# Revit family: ЭВАН ЭПВН 9,45-18 кВт
name_source: partatom
category: Оборудование
units: mm (PartAtom-declared; Revit-internal decimal feet)

## family parameters
Всегда вертикально = Да
Классификация = Нет
На основе рабочей плоскости = Да
Общий = Нет
При загрузке вырезать с полостями = Нет
Размер круглого соединителя = Использовать диаметр
Тип детали = Нормальный
Точка расчета площади = Нет

## types (4) — shared parameters
ADSK_Классификация нагрузок = Прочее
ADSK_Материал = Сталь
ADSK_Номинальная мощность = 0 Вт
ADSK_Размер_Высота = 346 мм
ADSK_Размер_Длина = 634 мм
ADSK_Размер_Ширина = 327 мм
Dn = 16 мм
База = ЭЛЕКТРИЧЕСКИЙ ТЕПЛОГЕНЕРАТОР (КОТЕЛ)
Крышка_Видимость = Да
Материал корпуса = Сталь
Минимально допустимое давление допустимое на входе в водонагреватель, МПа = 0.02
Мощность 1-й ступени (по умолчанию) = 0 Вт
Объем колбы котла, л = 7.5
Рабоча зона_Видимость = Да
Резьба патрубков для подключения трубопроводов теплоносителя = G 1/2
zero-valued in all types: Отметка по умолчанию

## per-type parameters (varying)
| type | ADSK_Количество фаз | ADSK_Расход теплоносителя | Максимальная температура теплоносителя, оС | Потребляемая электрическая мощность при максимальной тепловой мощность  в час, кВт/ч |
| ЭВАН ЭПВН - 9.45 кВт | 1 | 0.2 м³/ч | +65 | 7.87 |
| ЭВАН ЭПВН - 12 кВт | 3 | 0.3 м³/ч | +70 | 12.6 |
| ЭВАН ЭПВН - 15 кВт | 3 | 0.4 м³/ч | +67 | 15.75 |
| ЭВАН ЭПВН - 18 кВт | 3 | 0.5 м³/ч | +65 | 18.9 |
